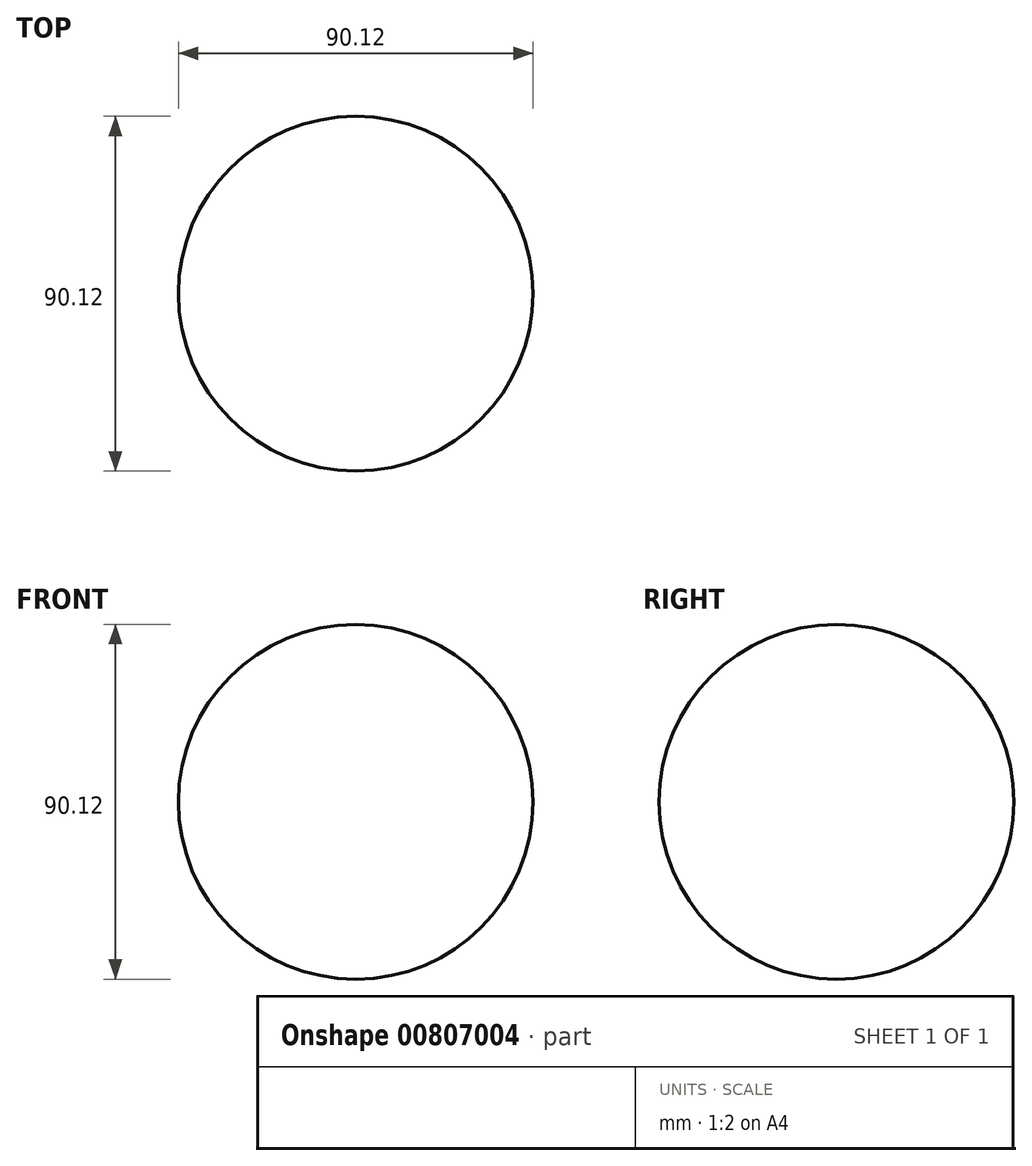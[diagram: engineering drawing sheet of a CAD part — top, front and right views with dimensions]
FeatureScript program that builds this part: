
annotation { "Feature Type Name" : "Feature", "Feature Type Description" : "" }
export const myFeature = defineFeature(function(context is Context, id is Id, definition is map)
    precondition{}
    {
        {
            var Q0;
            Q0=qCreatedBy(makeId("Front.planeOp"),FACE);
            var sketch = newSketch(context, id + "F0", { "sketchPlane" : qUnion([Q0])});
            skCircle(sketch, "E0", {"center": v(0, 0) * mm, "radius": 45.06 * mm});
            skLineSegment(sketch, "E1", {"start": v(0, 61.97) * mm, "end": v(0, -64.4) * mm});
            skSolve(sketch);
        }
        {
            var Q0;
            {var subQ0=sQuery(id+"F0.wireOp",EDGE,"E1");var subQ1=sQuery(id+"F0.wireOp",EDGE,"E0");var subQ2=makeQuery(id+"F0.imprint","INTERSECT",VERTEX,{"disambiguationData":[OD(0.0)],"derivedFrom":[subQ1,subQ0]});Q0=makeQuery(id+"F0.imprint","IMPRINT",FACE,{"disambiguationData":[TD([[makeQuery(id+"F0.imprint","IMPRINT",EDGE,{"disambiguationData":[TD([[subQ2,-1.0]])],"derivedFrom":subQ1}),1.0]])]});}
            var Q1;
            Q1=sQuery(id+"F0.wireOp",EDGE,"E1");
            revolve(context, id + "F1", {"surfaceOperationType" : NewSurfaceOperationType.NEW, "entities" : qUnion([Q0]), "axis" : qUnion([Q1]), "revolveType" : RevolveType.FULL});
        }
    });
